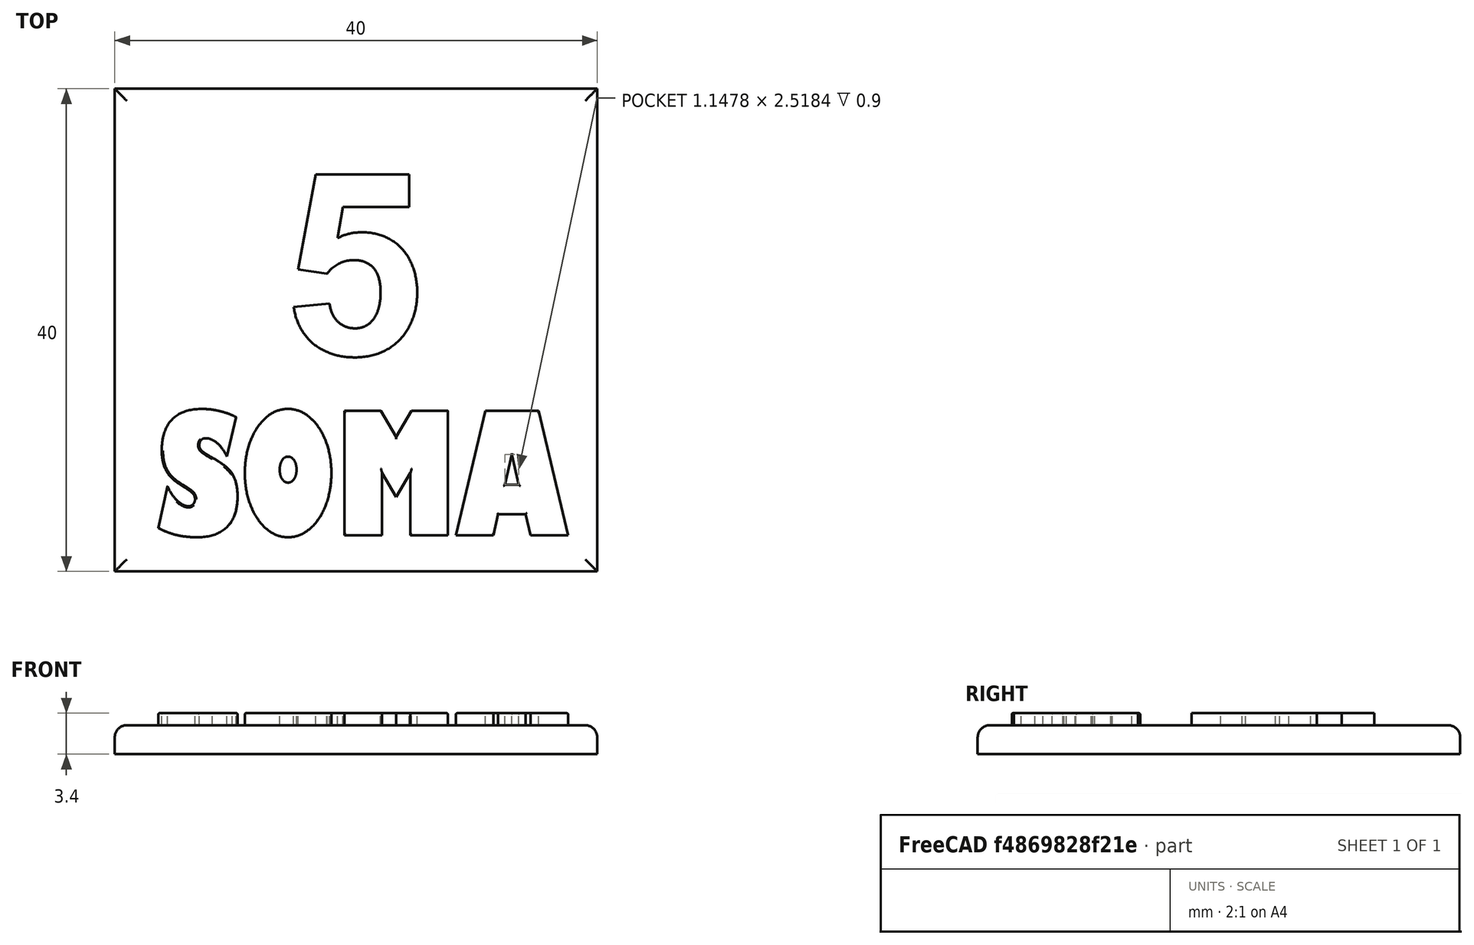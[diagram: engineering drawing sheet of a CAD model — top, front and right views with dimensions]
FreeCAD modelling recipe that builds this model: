
FCSTD DOCUMENT  (FreeCAD 0.21R33771 (Git))
Label: somaKg
License: All rights reserved
LicenseURL: http://en.wikipedia.org/wiki/All_rights_reserved
objects: Part::Part2DObjectPython×2, Part::Extrusion×2, Part::Fillet×2, Part::MultiFuse×2, Part::Box×1
note: 9 computed .brp shape members not serialized (recipe doc carries the construction recipe); baked Part::Feature solids carry a one-line shape summary decoded from their .brp

FEATURE [Part::Box] Box  label="Base"
  AttacherType = Attacher::AttachEngine3D
  Height = 2.4
  Length = 40
  Placement = pos=(4,0,0) rot=(0,0,1;0rad)
  Width = 40
FEATURE [Part::Part2DObjectPython] ShapeString  # Draft 2D object (typed FeaturePython)
  FontFile = <path>
  MakeFace = true
  Placement = pos=(8,5,2.4) rot=(0,0,1;0rad)
  Size = 12
  String = SOMA
  Tracking = 0
FEATURE [Part::Extrusion] Extrude  label="Soma"
  Base = -> ShapeString
  Dir = (0,0,1)
  DirMode = 2
  FaceMakerClass = Part::FaceMakerBullseye
  LengthFwd = 1
  LengthRev = 0
  Placement = pos=(-0.5,-2,0) rot=(0,0,1;0rad)
  Solid = true
  Symmetric = false
FEATURE [Part::Part2DObjectPython] ShapeString001  # Draft 2D object (typed FeaturePython)
  FontFile = <path>
  MakeFace = true
  Placement = pos=(18,18,2.4) rot=(0,0,1;0rad)
  Size = 17
  String = 5
  Tracking = -1
  expr: Tracking = -1
FEATURE [Part::Extrusion] Extrude001
  Base = -> ShapeString001
  Dir = (0,0,1)
  DirMode = 2
  FaceMakerClass = Part::FaceMakerBullseye
  LengthFwd = 1
  LengthRev = 0
  Solid = true
  Symmetric = false
FEATURE [Part::Fillet] Fillet
  Base = -> Box
  Edges = 4 edges r=1: [Edge2,Edge6,Edge10,Edge12]
FEATURE [Part::MultiFuse] Fusion
  Refine = true
  Shapes = -> [Fillet,Extrude001]
FEATURE [Part::Fillet] Fillet001
  Base = -> Extrude
  Edges = 71 edges r=0.1: [Edge4,Edge7,Edge10,Edge13,Edge16,Edge19,Edge22,Edge25,Edge28,Edge31,Edge34,Edge37,Edge40,Edge43,Edge46,Edge49,Edge52,Edge55,Edge58,Edge61,Edge64,Edge67,Edge70,Edge73,Edge76,Edge79,Edge82,Edge84,Edge88,Edge91,Edge94,Edge97,Edge100,Edge103,Edge106,Edge109,Edge112,Edge115,Edge118,Edge120,Edge124,+30 more]
FEATURE [Part::MultiFuse] Fusion001
  Refine = true
  Shapes = -> [Fillet001,Fusion]
note: 2 file-system paths scrubbed to <path> (originals preserved in the JSON sidecar)
